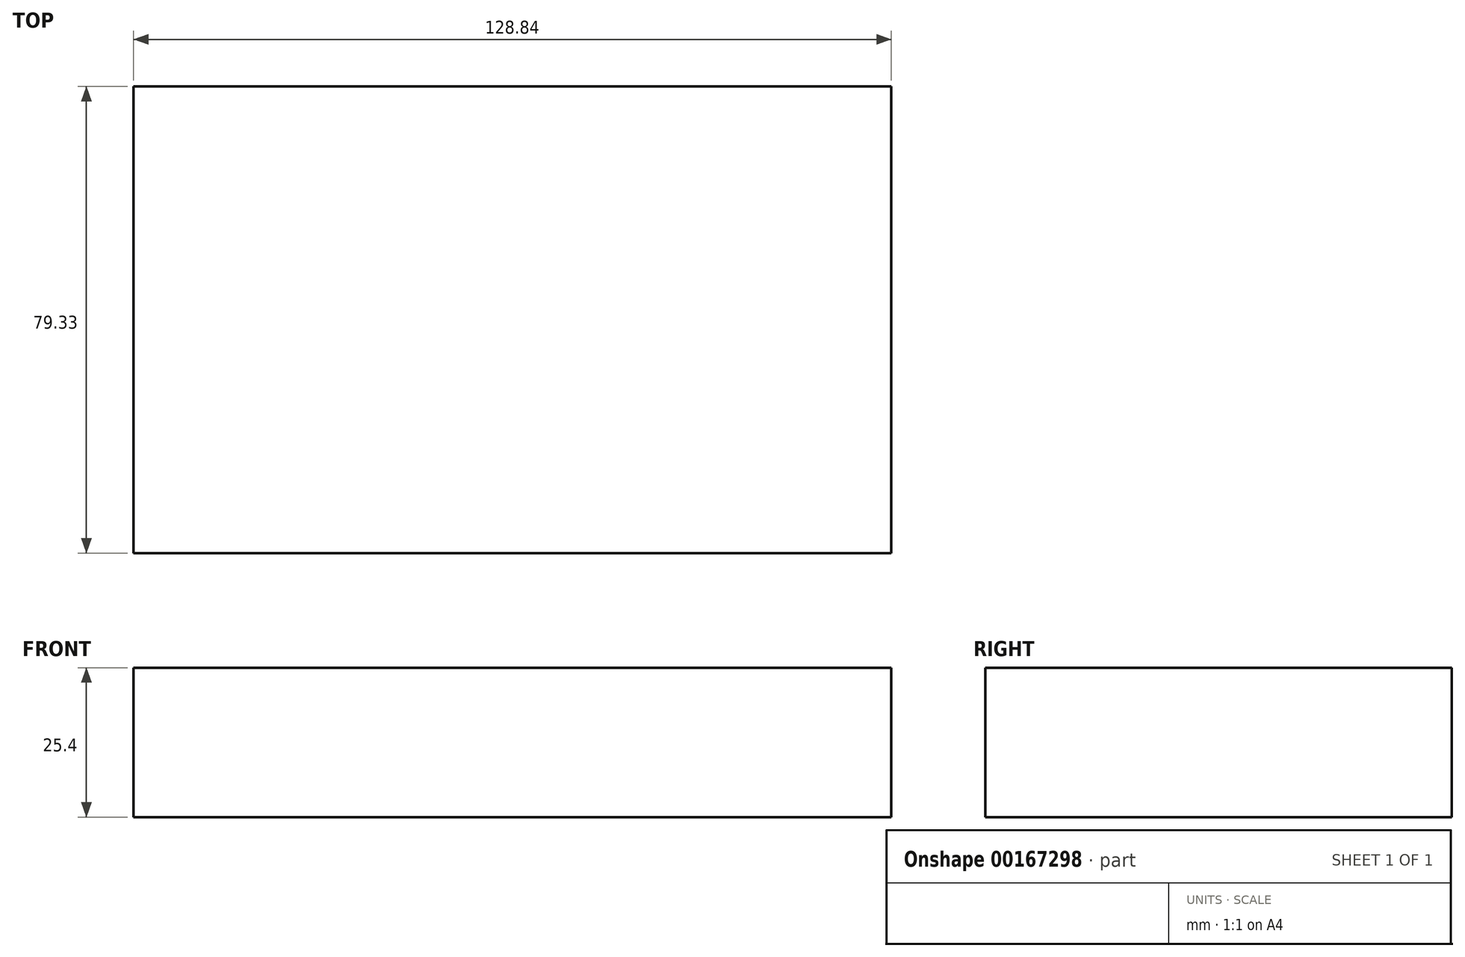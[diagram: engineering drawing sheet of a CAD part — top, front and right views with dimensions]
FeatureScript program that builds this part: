
annotation { "Feature Type Name" : "Feature", "Feature Type Description" : "" }
export const myFeature = defineFeature(function(context is Context, id is Id, definition is map)
    precondition{}
    {
        {
            var Q0;
            Q0=qCreatedBy(makeId("Top.planeOp"),FACE);
            var sketch = newSketch(context, id + "F0", { "sketchPlane" : qUnion([Q0])});
            skLineSegment(sketch, "E0.bottom", {"start": v(-144, 52.03) * mm, "end": v(-15.16, 52.03) * mm});
            skLineSegment(sketch, "E0.top", {"start": v(-144, -27.3) * mm, "end": v(-15.16, -27.3) * mm});
            skLineSegment(sketch, "E0.left", {"start": v(-144, 52.03) * mm, "end": v(-144, -27.3) * mm});
            skLineSegment(sketch, "E0.right", {"start": v(-15.16, 52.03) * mm, "end": v(-15.16, -27.3) * mm});
            skSolve(sketch);
        }
        {
            var Q0;
            Q0=qSketchRegion(id+"F0",true);
            extrude(context, id + "F1", {"entities" : qUnion([Q0]), "depth" : 25.4 * mm});
        }
    });
